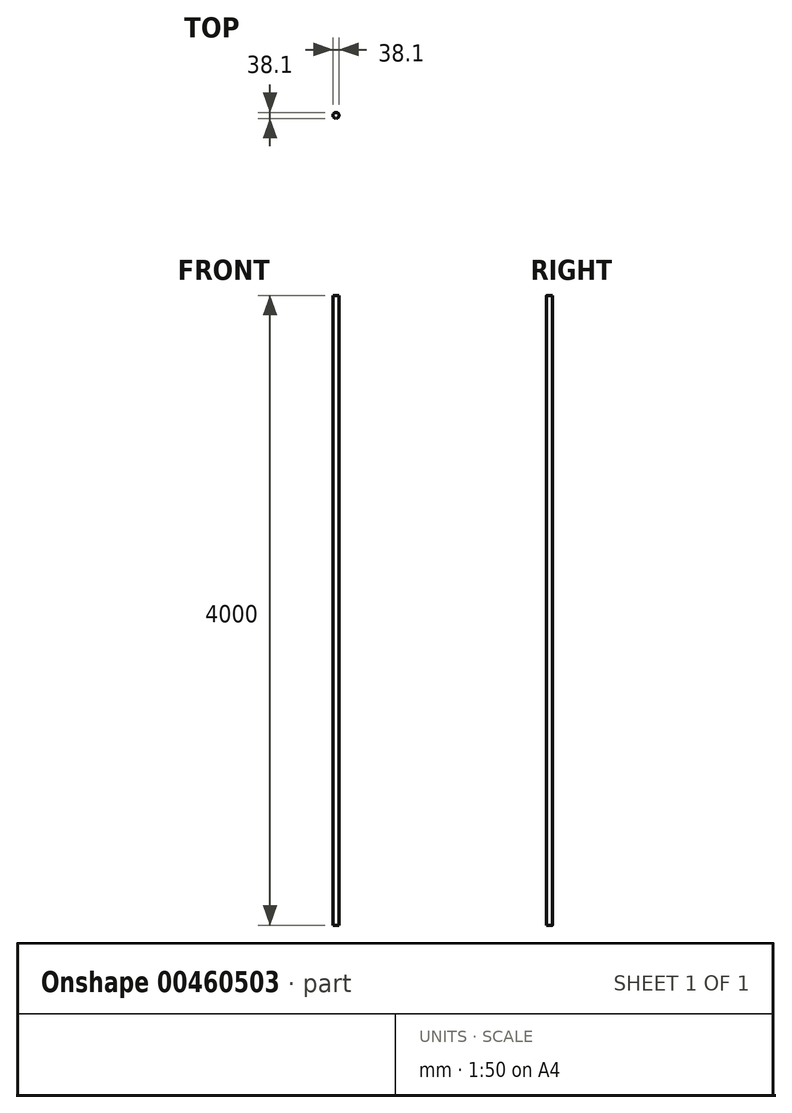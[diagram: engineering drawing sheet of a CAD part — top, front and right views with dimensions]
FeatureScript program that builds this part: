
annotation { "Feature Type Name" : "Feature", "Feature Type Description" : "" }
export const myFeature = defineFeature(function(context is Context, id is Id, definition is map)
    precondition{}
    {
        {
            var Q0;
            Q0=qCreatedBy(makeId("Top.planeOp"),FACE);
            var sketch = newSketch(context, id + "F0", { "sketchPlane" : qUnion([Q0])});
            skCircle(sketch, "E0", {"center": v(0, 0) * mm, "radius": 19.05 * mm});
            skSolve(sketch);
        }
        {
            var Q0;
            Q0 = qSketchRegion(id + "F0", true);
            extrude(context, id + "F1", {"entities" : qUnion([Q0]), "depth" : 4000 * mm});
        }
    });
